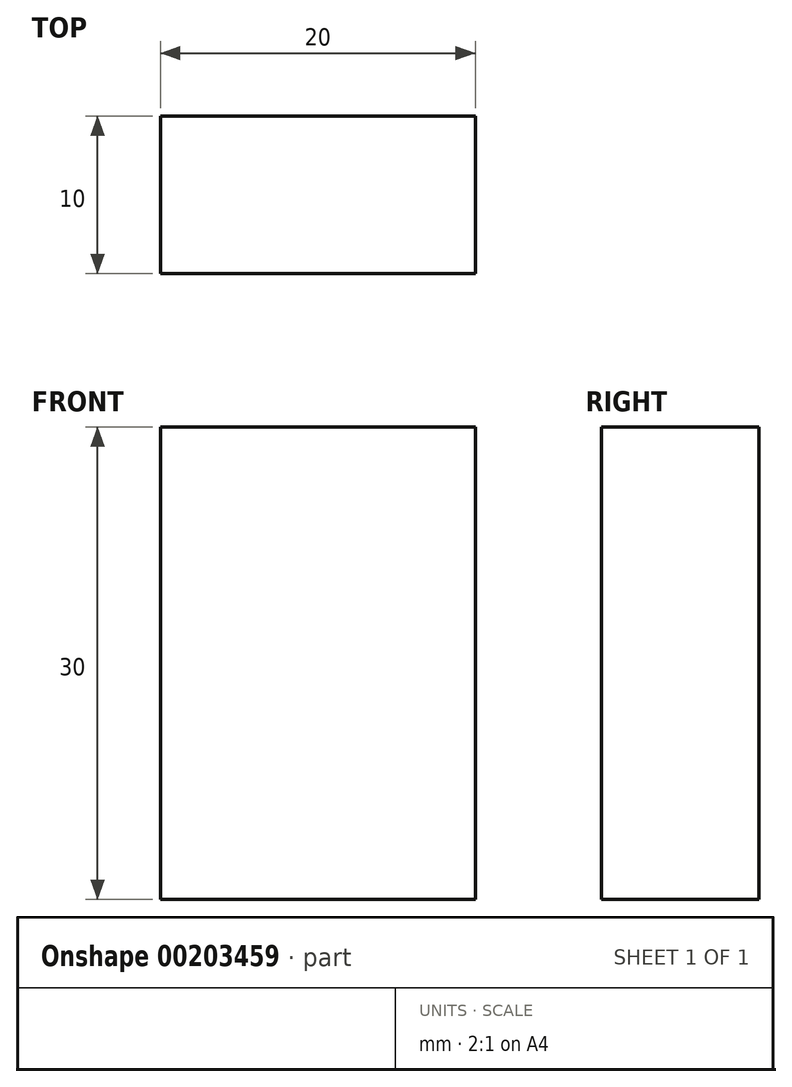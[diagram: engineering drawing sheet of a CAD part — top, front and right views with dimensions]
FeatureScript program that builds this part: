
annotation { "Feature Type Name" : "Feature", "Feature Type Description" : "" }
export const myFeature = defineFeature(function(context is Context, id is Id, definition is map)
    precondition{}
    {
        {
            var Q0;
            Q0=qCreatedBy(makeId("Top.planeOp"),FACE);
            var sketch = newSketch(context, id + "F0", { "sketchPlane" : qUnion([Q0])});
            skLineSegment(sketch, "E0.bottom", {"start": v(-13.86, 4.91) * mm, "end": v(6.14, 4.91) * mm});
            skLineSegment(sketch, "E0.top", {"start": v(-13.86, -5.09) * mm, "end": v(6.14, -5.09) * mm});
            skLineSegment(sketch, "E0.left", {"start": v(-13.86, 4.91) * mm, "end": v(-13.86, -5.09) * mm});
            skLineSegment(sketch, "E0.right", {"start": v(6.14, 4.91) * mm, "end": v(6.14, -5.09) * mm});
            skSolve(sketch);
        }
        {
            var Q0;
            Q0 = qSketchRegion(id + "F0", true);
            extrude(context, id + "F1", {"entities" : qUnion([Q0]), "depth" : 30 * mm});
        }
    });
